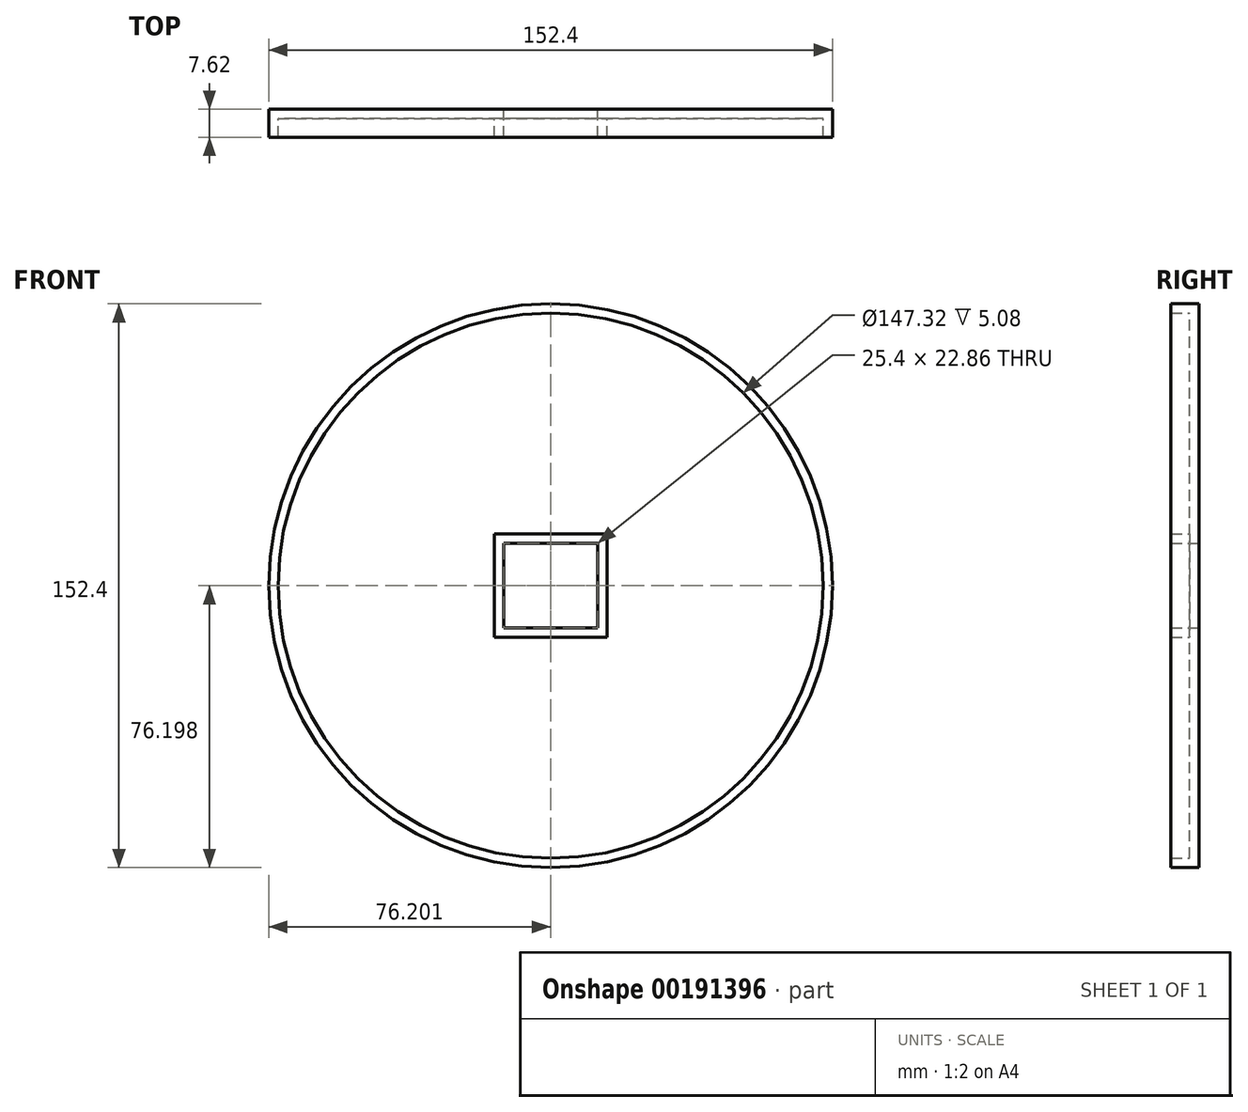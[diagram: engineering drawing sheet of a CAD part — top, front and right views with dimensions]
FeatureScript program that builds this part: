
annotation { "Feature Type Name" : "Feature", "Feature Type Description" : "" }
export const myFeature = defineFeature(function(context is Context, id is Id, definition is map)
    precondition{}
    {
        {
            var Q0;
            Q0=qCreatedBy(makeId("Front.planeOp"),FACE);
            var sketch = newSketch(context, id + "F0", { "sketchPlane" : qUnion([Q0])});
            skCircle(sketch, "E0", {"center": v(40.92, 25.09) * mm, "radius": 76.2 * mm});
            skLineSegment(sketch, "E1.bottom", {"start": v(53.62, 36.52) * mm, "end": v(28.22, 36.52) * mm});
            skLineSegment(sketch, "E1.top", {"start": v(53.62, 13.66) * mm, "end": v(28.22, 13.66) * mm});
            skLineSegment(sketch, "E1.left", {"start": v(53.62, 36.52) * mm, "end": v(53.62, 13.66) * mm});
            skLineSegment(sketch, "E1.right", {"start": v(28.22, 36.52) * mm, "end": v(28.22, 13.66) * mm});
            skSolve(sketch);
        }
        {
            var Q0;
            Q0=makeQuery(id+"F0.imprint","IMPRINT",FACE,{"disambiguationData":[TD([[makeQuery(id+"F0.imprint","IMPRINT",EDGE,{"derivedFrom":sQuery(id+"F0.wireOp",EDGE,"E0")}),1.0]])]});
            extrude(context, id + "F1", {"entities" : qUnion([Q0]), "depth" : 7.62 * mm});
        }
        {
            var Q0;
            Q0=sQuery(id+"F0.wireOp",EDGE,"E1.left");
            var Q1;
            Q1=sQuery(id+"F0.wireOp",EDGE,"E1.bottom");
            var Q2;
            Q2=sQuery(id+"F0.wireOp",EDGE,"E1.top");
            var Q3;
            Q3=sQuery(id+"F0.wireOp",EDGE,"E1.right");
            extrude(context, id + "F2", {"bodyType" : ToolBodyType.SURFACE, "surfaceEntities" : qUnion([Q0, Q1, Q2, Q3]), "oppositeDirection" : true, "depth" : 12.7 * mm});
        }
        {
            var Q0;
            Q0=makeQuery(id+"F1.opExtrude","CAP_FACE",FACE,{"disambiguationData":[OSD([sQuery(id+"F0.wireOp",EDGE,"E0"),sQuery(id+"F0.wireOp",EDGE,"dAvEYh1x-26gr-okKI-XZtd-vjtAiYHOEHgk")])],"isStart":false});
            shell(context, id + "F3", {"entities" : qUnion([Q0]), "thickness" : 2.54 * mm});
        }
    });
